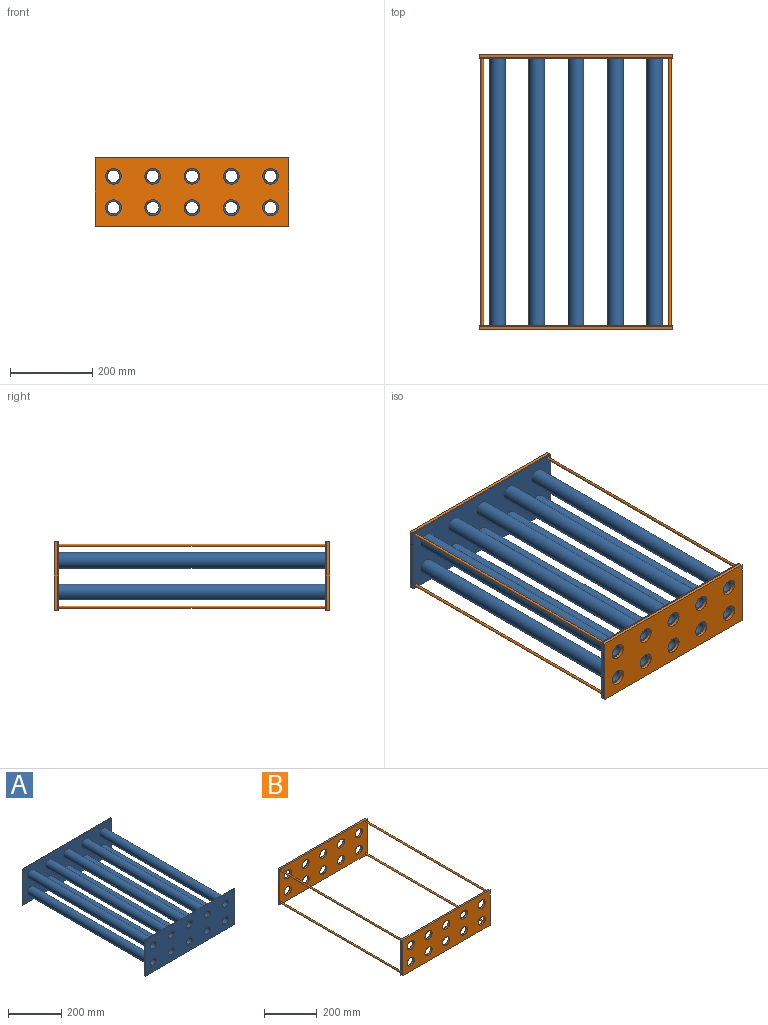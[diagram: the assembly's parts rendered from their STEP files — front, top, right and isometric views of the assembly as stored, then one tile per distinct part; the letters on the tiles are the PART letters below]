
ASSEMBLY  parts=2 mates=1
PART A: 40 faces, bbox 469.9x652x165.1 mm
  f0: cylinder r=19.05mm len=646.94mm, axis (0,-1,0), area 77435mm2, adj f30,f39
  f1: plane 469.9x165.1mm, normal (0,1,0), area 70157.2mm2, adj f2,f5,f7,f9,f11,f13,f15,f17
  f2: cylinder r=15.24mm len=652.02mm, axis (0,-1,0), area 62434.5mm2, adj f1,f3
  f3: plane 469.9x165.1mm, normal (0,-1,0), area 70157.2mm2, adj f2,f5,f7,f9,f11,f13,f15,f17
  f4: cylinder r=19.05mm len=646.94mm, axis (0,-1,0), area 77435mm2, adj f30,f39
  f5: cylinder r=15.24mm len=652.02mm, axis (0,-1,0), area 62434.5mm2, adj f1,f3
  f6: cylinder r=19.05mm len=646.94mm, axis (0,-1,0), area 77435mm2, adj f30,f39
  f7: cylinder r=15.24mm len=652.02mm, axis (0,-1,0), area 62434.5mm2, adj f1,f3
  f8: cylinder r=19.05mm len=646.94mm, axis (0,-1,0), area 77435mm2, adj f30,f39
  f9: cylinder r=15.24mm len=652.02mm, axis (0,-1,0), area 62434.5mm2, adj f1,f3
  f10: cylinder r=19.05mm len=646.94mm, axis (0,-1,0), area 77435mm2, adj f30,f39
  f11: cylinder r=15.24mm len=652.02mm, axis (0,-1,0), area 62434.5mm2, adj f1,f3
  f12: cylinder r=19.05mm len=646.94mm, axis (0,-1,0), area 77435mm2, adj f30,f39
  f13: cylinder r=15.24mm len=652.02mm, axis (0,-1,0), area 62434.5mm2, adj f1,f3
  f14: cylinder r=19.05mm len=646.94mm, axis (0,-1,0), area 77435mm2, adj f30,f39
  f15: cylinder r=15.24mm len=652.02mm, axis (0,-1,0), area 62434.5mm2, adj f1,f3
  f16: cylinder r=19.05mm len=646.94mm, axis (0,-1,0), area 77435mm2, adj f30,f39
  f17: cylinder r=15.24mm len=652.02mm, axis (0,-1,0), area 62434.5mm2, adj f1,f3
  f18: cylinder r=19.05mm len=646.94mm, axis (0,-1,0), area 77435mm2, adj f30,f39
  f19: cylinder r=15.24mm len=652.02mm, axis (0,-1,0), area 62434.5mm2, adj f1,f3
  f20: cylinder r=19.05mm len=646.94mm, axis (0,-1,0), area 77435mm2, adj f30,f39
  f21: cylinder r=15.24mm len=652.02mm, axis (0,-1,0), area 62434.5mm2, adj f1,f3
  f22: plane 165.1x2.54mm, normal (-1,0,0), area 419.4mm2, adj f3,f23,f29,f30
  f23: plane 469.9x2.54mm, normal (0,0,-1), area 1193.5mm2, adj f3,f22,f24,f30
  f24: plane 165.1x2.54mm, normal (1,0,0), area 419.4mm2, adj f3,f23,f29,f30
  f25: cylinder r=3.17mm len=6.35mm, axis (0,-1,0), area 50.7mm2, adj f3,f30
  f26: cylinder r=3.17mm len=6.35mm, axis (0,-1,0), area 50.7mm2, adj f3,f30
  f27: cylinder r=3.17mm len=6.35mm, axis (0,-1,0), area 50.7mm2, adj f3,f30
  f28: cylinder r=3.17mm len=6.35mm, axis (0,-1,0), area 50.7mm2, adj f3,f30
  f29: plane 469.9x2.54mm, normal (0,0,1), area 1193.5mm2, adj f3,f22,f24,f30
  f30: plane 469.9x165.1mm, normal (0,1,0), area 66052.9mm2, adj f0,f4,f6,f8,f10,f12,f14,f16
  f31: plane 165.1x2.54mm, normal (-1,0,0), area 419.4mm2, adj f1,f32,f38,f39
  f32: plane 469.9x2.54mm, normal (0,0,-1), area 1193.5mm2, adj f1,f31,f33,f39
  f33: plane 165.1x2.54mm, normal (1,0,0), area 419.4mm2, adj f1,f32,f38,f39
  f34: cylinder r=3.17mm len=6.35mm, axis (0,1,0), area 50.7mm2, adj f1,f39
  f35: cylinder r=3.17mm len=6.35mm, axis (0,1,0), area 50.7mm2, adj f1,f39
  f36: cylinder r=3.17mm len=6.35mm, axis (0,1,0), area 50.7mm2, adj f1,f39
  f37: cylinder r=3.17mm len=6.35mm, axis (0,1,0), area 50.7mm2, adj f1,f39
  f38: plane 469.9x2.54mm, normal (0,0,1), area 1193.5mm2, adj f1,f31,f33,f39
  f39: plane 469.9x165.1mm, normal (0,-1,0), area 66052.9mm2, adj f0,f4,f6,f8,f10,f12,f14,f16
PART B: 36 faces, bbox 469.9x668.8x165.1 mm
  f0: plane 165.1x8.38mm, normal (-1,0,0), area 1383.9mm2, adj f1,f12,f14,f15
  f1: plane 469.9x8.38mm, normal (0,0,-1), area 3938.7mm2, adj f0,f2,f14,f15
  f2: plane 165.1x8.38mm, normal (1,0,0), area 1383.9mm2, adj f1,f12,f14,f15
  f3: cylinder r=19.05mm len=38.1mm, axis (0,1,0), area 1003.3mm2, adj f14,f15
  f4: cylinder r=19.05mm len=38.1mm, axis (0,1,0), area 1003.3mm2, adj f14,f15
  f5: cylinder r=19.05mm len=38.1mm, axis (0,1,0), area 1003.3mm2, adj f14,f15
  f6: cylinder r=19.05mm len=38.1mm, axis (0,1,0), area 1003.3mm2, adj f14,f15
  f7: cylinder r=19.05mm len=38.1mm, axis (0,1,0), area 1003.3mm2, adj f14,f15
  f8: cylinder r=19.05mm len=38.1mm, axis (0,1,0), area 1003.3mm2, adj f14,f15
  f9: cylinder r=19.05mm len=38.1mm, axis (0,1,0), area 1003.3mm2, adj f14,f15
  f10: cylinder r=19.05mm len=38.1mm, axis (0,1,0), area 1003.3mm2, adj f14,f15
  f11: cylinder r=19.05mm len=38.1mm, axis (0,1,0), area 1003.3mm2, adj f14,f15
  f12: plane 469.9x8.38mm, normal (0,0,1), area 3938.7mm2, adj f0,f2,f14,f15
  f13: cylinder r=19.05mm len=38.1mm, axis (0,1,0), area 1003.3mm2, adj f14,f15
  f14: plane 469.9x165.1mm, normal (0,-1,0), area 66179.6mm2, adj f0,f1,f2,f3,f4,f5,f6,f7
  f15: plane 469.9x165.1mm, normal (0,1,0), area 66052.9mm2, adj f0,f1,f2,f3,f4,f5,f6,f7
  f16: plane 469.9x165.1mm, normal (0,1,0), area 66179.6mm2, adj f18,f19,f20,f21,f22,f23,f24,f25
  f17: plane 469.9x165.1mm, normal (0,-1,0), area 66052.9mm2, adj f18,f19,f20,f21,f22,f23,f24,f25
  f18: cylinder r=19.05mm len=38.1mm, axis (0,1,0), area 1003.3mm2, adj f16,f17
  f19: plane 469.9x8.38mm, normal (0,0,1), area 3938.7mm2, adj f16,f17,f29,f31
  f20: cylinder r=19.05mm len=38.1mm, axis (0,1,0), area 1003.3mm2, adj f16,f17
  f21: cylinder r=19.05mm len=38.1mm, axis (0,1,0), area 1003.3mm2, adj f16,f17
  f22: cylinder r=19.05mm len=38.1mm, axis (0,1,0), area 1003.3mm2, adj f16,f17
  f23: cylinder r=19.05mm len=38.1mm, axis (0,1,0), area 1003.3mm2, adj f16,f17
  f24: cylinder r=19.05mm len=38.1mm, axis (0,1,0), area 1003.3mm2, adj f16,f17
  f25: cylinder r=19.05mm len=38.1mm, axis (0,1,0), area 1003.3mm2, adj f16,f17
  f26: cylinder r=19.05mm len=38.1mm, axis (0,1,0), area 1003.3mm2, adj f16,f17
  f27: cylinder r=19.05mm len=38.1mm, axis (0,1,0), area 1003.3mm2, adj f16,f17
  f28: cylinder r=19.05mm len=38.1mm, axis (0,1,0), area 1003.3mm2, adj f16,f17
  f29: plane 165.1x8.38mm, normal (1,0,0), area 1383.9mm2, adj f16,f17,f19,f30
  f30: plane 469.9x8.38mm, normal (0,0,-1), area 3938.7mm2, adj f16,f17,f29,f31
  f31: plane 165.1x8.38mm, normal (-1,0,0), area 1383.9mm2, adj f16,f17,f19,f30
  f32: cylinder r=3.17mm len=652.02mm, axis (0,-1,0), area 13007.2mm2, adj f15,f17
  f33: cylinder r=3.17mm len=652.02mm, axis (0,-1,0), area 13007.2mm2, adj f15,f17
  f34: cylinder r=3.17mm len=652.02mm, axis (0,-1,0), area 13007.2mm2, adj f15,f17
  f35: cylinder r=3.17mm len=652.02mm, axis (0,-1,0), area 13007.2mm2, adj f15,f17
PLACE A t=(-207.79,-363.57,123.61)mm
PLACE B t=(-207.79,-363.57,123.61)mm
MATE fastened B.f17 <-> A.f1  axis (0,-1,0) through (-207.79,288.45,123.61)mm
